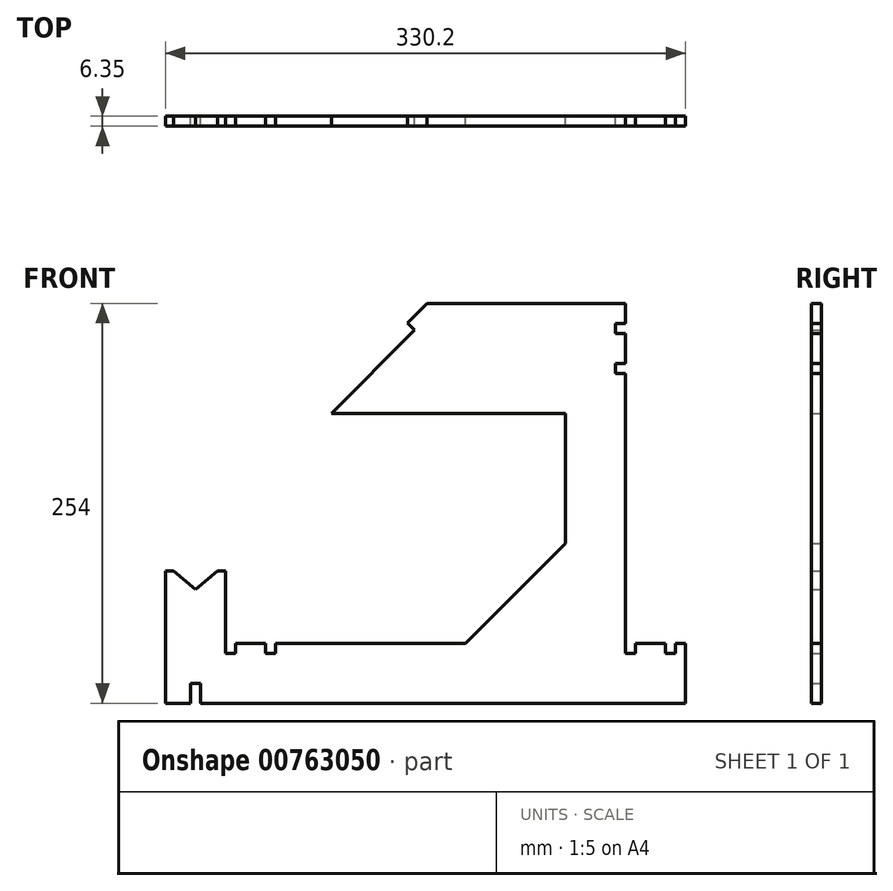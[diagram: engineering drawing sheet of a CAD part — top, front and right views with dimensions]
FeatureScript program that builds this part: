
annotation { "Feature Type Name" : "Feature", "Feature Type Description" : "" }
export const myFeature = defineFeature(function(context is Context, id is Id, definition is map)
    precondition{}
    {
        {
            var Q0;
            Q0=qCreatedBy(makeId("Front.planeOp"),FACE);
            var sketch = newSketch(context, id + "F0", { "sketchPlane" : qUnion([Q0])});
            skLineSegment(sketch, "E0", {"start": v(-82.64, -105.94) * mm, "end": v(-146.14, -169.44) * mm});
            skLineSegment(sketch, "E1", {"start": v(-146.14, -169.44) * mm, "end": v(-266.8, -169.44) * mm});
            skLineSegment(sketch, "E2", {"start": v(-336.64, -207.54) * mm, "end": v(-336.64, -123.4) * mm});
            skCircle(sketch, "E3", {"center": v(-317.6, -118.64) * mm, "radius": 12.7 * mm, "construction": true});
            skLineSegment(sketch, "E4.0", {"start": v(-336.64, -123.4) * mm, "end": v(-331.67, -123.4) * mm});
            skLineSegment(sketch, "E5", {"start": v(-298.54, -123.4) * mm, "end": v(-298.54, -175.79) * mm});
            skLineSegment(sketch, "E6.trimOffspring", {"start": v(-303.5, -123.4) * mm, "end": v(-298.54, -123.4) * mm});
            skPoint(sketch, "E7.orphan", {"position": v(-317.6, -130.6) * mm});
            skLineSegment(sketch, "E8.0", {"start": v(-331.67, -123.4) * mm, "end": v(-317.6, -135.21) * mm});
            skLineSegment(sketch, "E9.0", {"start": v(-303.5, -123.4) * mm, "end": v(-317.6, -135.21) * mm});
            skLineSegment(sketch, "E10", {"start": v(-325.75, -128.36) * mm, "end": v(-317.6, -118.64) * mm, "construction": true});
            skLineSegment(sketch, "E11", {"start": v(-309.43, -128.36) * mm, "end": v(-317.6, -118.64) * mm, "construction": true});
            skLineSegment(sketch, "E12.0", {"start": v(-6.44, -207.54) * mm, "end": v(-314.42, -207.54) * mm});
            skLineSegment(sketch, "E13", {"start": v(-44.54, 46.46) * mm, "end": v(-44.54, 33.76) * mm});
            skLineSegment(sketch, "E14", {"start": v(-38.2, -169.44) * mm, "end": v(-19.14, -169.44) * mm});
            skLineSegment(sketch, "E15", {"start": v(-6.44, -169.44) * mm, "end": v(-6.44, -207.54) * mm});
            skLineSegment(sketch, "E16", {"start": v(-82.64, -105.94) * mm, "end": v(-82.64, -23.39) * mm});
            skLineSegment(sketch, "E17", {"start": v(-231.32, -23.39) * mm, "end": v(-82.64, -23.39) * mm});
            skLineSegment(sketch, "E18.0", {"start": v(-170.45, 46.46) * mm, "end": v(-44.54, 46.46) * mm});
            skLineSegment(sketch, "E19.top", {"start": v(-320.77, -194.84) * mm, "end": v(-314.42, -194.84) * mm});
            skLineSegment(sketch, "E19.left", {"start": v(-320.77, -207.54) * mm, "end": v(-320.77, -194.84) * mm});
            skLineSegment(sketch, "E19.right", {"start": v(-314.42, -207.54) * mm, "end": v(-314.42, -194.84) * mm});
            skLineSegment(sketch, "E20.trimOffspring", {"start": v(-320.77, -207.54) * mm, "end": v(-336.64, -207.54) * mm});
            skLineSegment(sketch, "E21.top", {"start": v(-298.54, -175.79) * mm, "end": v(-292.2, -175.79) * mm});
            skLineSegment(sketch, "E21.right", {"start": v(-292.2, -169.44) * mm, "end": v(-292.2, -175.79) * mm});
            skLineSegment(sketch, "E22.bottom", {"start": v(-273.14, -175.79) * mm, "end": v(-266.8, -175.79) * mm});
            skLineSegment(sketch, "E22.left", {"start": v(-273.14, -175.79) * mm, "end": v(-273.14, -169.44) * mm});
            skLineSegment(sketch, "E22.right", {"start": v(-266.8, -175.79) * mm, "end": v(-266.8, -169.44) * mm});
            skLineSegment(sketch, "E23.trimOffspring", {"start": v(-273.14, -169.44) * mm, "end": v(-292.2, -169.44) * mm});
            skLineSegment(sketch, "E24.top", {"start": v(-44.54, -175.79) * mm, "end": v(-38.2, -175.79) * mm});
            skLineSegment(sketch, "E24.right", {"start": v(-38.2, -169.44) * mm, "end": v(-38.2, -175.79) * mm});
            skLineSegment(sketch, "E25.bottom", {"start": v(-19.14, -175.79) * mm, "end": v(-12.8, -175.79) * mm});
            skLineSegment(sketch, "E25.left", {"start": v(-19.14, -175.79) * mm, "end": v(-19.14, -169.44) * mm});
            skLineSegment(sketch, "E25.right", {"start": v(-12.8, -175.79) * mm, "end": v(-12.8, -169.44) * mm});
            skLineSegment(sketch, "E26.trimOffspring", {"start": v(-12.8, -169.44) * mm, "end": v(-6.44, -169.44) * mm});
            skLineSegment(sketch, "E27.bottom", {"start": v(-44.54, 33.76) * mm, "end": v(-50.9, 33.76) * mm});
            skLineSegment(sketch, "E27.top", {"start": v(-44.54, 27.41) * mm, "end": v(-50.9, 27.41) * mm});
            skLineSegment(sketch, "E27.right", {"start": v(-50.9, 33.76) * mm, "end": v(-50.9, 27.41) * mm});
            skLineSegment(sketch, "E28.bottom", {"start": v(-50.9, 8.36) * mm, "end": v(-44.54, 8.36) * mm});
            skLineSegment(sketch, "E28.top", {"start": v(-50.9, 2.01) * mm, "end": v(-44.54, 2.01) * mm});
            skLineSegment(sketch, "E28.left", {"start": v(-50.9, 8.36) * mm, "end": v(-50.9, 2.01) * mm});
            skLineSegment(sketch, "E29.trimOffspring", {"start": v(-44.54, 27.41) * mm, "end": v(-44.54, 8.36) * mm});
            skLineSegment(sketch, "E30.trimOffspring", {"start": v(-44.54, 2.01) * mm, "end": v(-44.54, -175.79) * mm});
            skLineSegment(sketch, "E31", {"start": v(-317.6, -118.64) * mm, "end": v(-298.07, -99.11) * mm, "construction": true});
            skLineSegment(sketch, "E32.0", {"start": v(-326.57, -109.66) * mm, "end": v(-182.89, 34.03) * mm, "construction": true});
            skLineSegment(sketch, "E33", {"start": v(-182.89, 34.03) * mm, "end": v(-178.4, 29.54) * mm});
            skLineSegment(sketch, "E34", {"start": v(-182.89, 34.03) * mm, "end": v(-170.45, 46.46) * mm});
            skLineSegment(sketch, "E35.trimOffspring", {"start": v(-231.32, -23.39) * mm, "end": v(-178.4, 29.54) * mm});
            skSolve(sketch);
        }
        {
            var Q0;
            Q0 = qSketchRegion(id + "F0", true);
            extrude(context, id + "F1", {"entities" : qUnion([Q0]), "depth" : 6.35 * mm, "offsetDistance" : 25.4 * mm});
        }
    });
